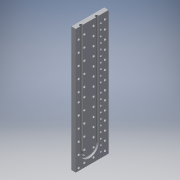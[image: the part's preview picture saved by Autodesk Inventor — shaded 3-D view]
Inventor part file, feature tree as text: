
AUTODESK INVENTOR PART (.ipt)
format: ipt  version: 2016 SP2 (Build 200236200, 236)  size: 468,992 bytes
history: native  units: mm
features: sketch x4, reference x3, hole x2, projected_geometry x2, extrude x1, sweep x1, plane x1
ambient origin geometry x8: Origin, YZ Plane, XZ Plane, XY Plane, X Axis, Y Axis, Z Axis, Center Point
bodies: Solid1 (feature_tree)
feature tree (14):
  extrude  "Extrusion1"  Depth=10.0mm
  hole  "Hole1"  [1 undecoded]
  sweep  "Sweep1"
  hole  "Hole2"  [1 undecoded]
  plane  "Work Plane1"
  sketch  "Sketch10"  dims[d11=36.0mm d12=34.0mm d13=0.0mm d14=0.0mm d17=5.3mm d18=6.0mm d19=4.0mm d20=2.0mm d21=90.0deg d22=8.0mm d23=20.594885mm d24=4.0mm d25=6.0mm d26=4.0mm d27=2.0mm d28=90.0deg d29=8.0mm d30=20.594885mm]
  sketch  "Sketch1"  dims[d0=75.0mm d1=10.0mm]
  sketch  "Sketch2"  dims[d2=284.0mm d3=0.0mm d4=6.0mm]
  projected_geometry  "Projected Loop1"
  sketch  "Sketch3"  dims[d5=2.0mm d6=12.0mm]
  reference  "Reference2"
  reference  "Reference3"
  reference  "Reference4"
  projected_geometry  "Project Cut Edges1"
note: 2 required parameter values undecoded (feature->parameter linkage not recoverable at this tier; creation-order binding heuristic only, values carry confidence <= 0.55)
